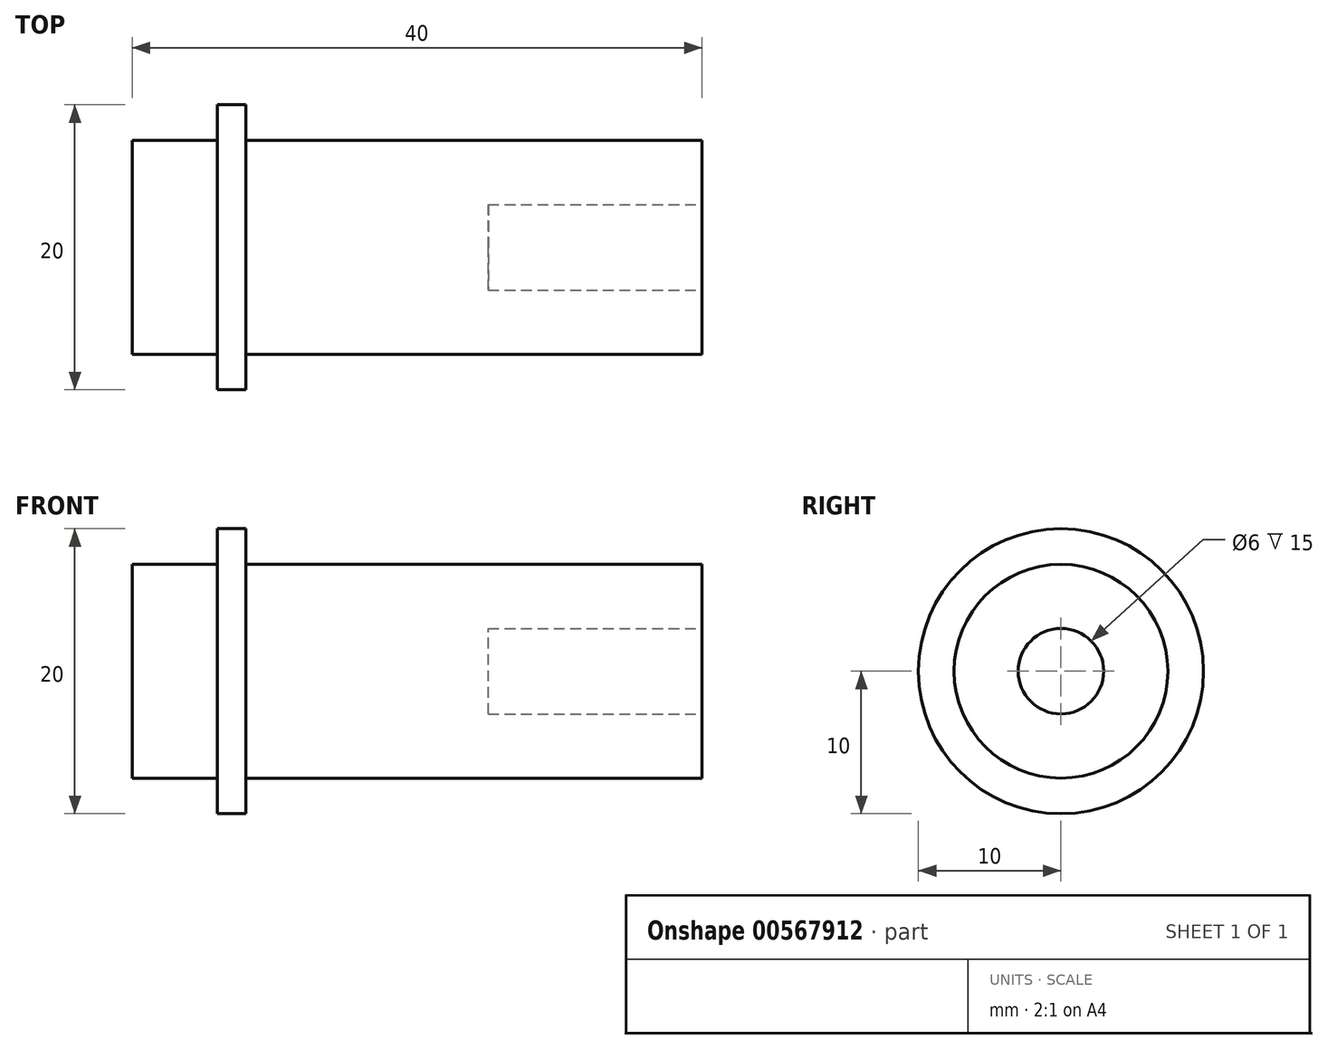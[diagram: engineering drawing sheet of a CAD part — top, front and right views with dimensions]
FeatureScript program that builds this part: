
annotation { "Feature Type Name" : "Feature", "Feature Type Description" : "" }
export const myFeature = defineFeature(function(context is Context, id is Id, definition is map)
    precondition{}
    {
        {
            var Q0;
            Q0=qCreatedBy(makeId("Front.planeOp"),FACE);
            var sketch = newSketch(context, id + "F0", { "sketchPlane" : qUnion([Q0])});
            skLineSegment(sketch, "E0", {"start": v(0, 0) * mm, "end": v(40, 0) * mm});
            skLineSegment(sketch, "E1", {"start": v(40, 0) * mm, "end": v(40, -7.5) * mm});
            skLineSegment(sketch, "E2", {"start": v(40, -7.5) * mm, "end": v(8, -7.5) * mm});
            skLineSegment(sketch, "E3", {"start": v(8, -7.5) * mm, "end": v(8, -10) * mm});
            skLineSegment(sketch, "E4", {"start": v(8, -10) * mm, "end": v(6, -10) * mm});
            skLineSegment(sketch, "E5", {"start": v(6, -10) * mm, "end": v(6, -7.5) * mm});
            skLineSegment(sketch, "E6", {"start": v(6, -7.5) * mm, "end": v(0, -7.5) * mm});
            skLineSegment(sketch, "E7", {"start": v(0, -7.5) * mm, "end": v(0, 0) * mm});
            skSolve(sketch);
        }
        {
            var Q0;
            Q0=makeQuery(id+"F0.imprint","IMPRINT",FACE,{"disambiguationData":[TD([[makeQuery(id+"F0.imprint","IMPRINT",EDGE,{"derivedFrom":sQuery(id+"F0.wireOp",EDGE,"E0")}),-1.0]])]});
            var Q1;
            Q1=sQuery(id+"F0.wireOp",EDGE,"E0");
            revolve(context, id + "F1", {"entities" : qUnion([Q0]), "axis" : qUnion([Q1]), "revolveType" : RevolveType.FULL});
        }
        {
            var Q0;
            Q0=makeQuery(id+"F1.opRevolve","SWEPT_FACE",FACE,{"disambiguationData":[OSD([sQuery(id+"F0.wireOp",EDGE,"E1")])]});
            var sketch = newSketch(context, id + "F2", { "sketchPlane" : qUnion([Q0])});
            skCircle(sketch, "E8", {"center": v(0, 0) * mm, "radius": 3 * mm});
            skSolve(sketch);
        }
        {
            var Q0;
            Q0 = qSketchRegion(id + "F2", true);
            extrude(context, id + "F3", {"entities" : qUnion([Q0]), "operationType" : NewBodyOperationType.REMOVE, "oppositeDirection" : true, "depth" : 15 * mm, "offsetDistance" : 25 * mm});
        }
    });
